# Revit family: LZWS-EDFPBM114K
name_source: partatom
category: Plumbing Fixtures
units: mm (PartAtom-declared; Revit-internal decimal feet)

## family parameters
Always vertical = Yes
Cut with Voids When Loaded = No
OmniClass Number = 23.45.00.00
OmniClass Title = Sanitary, Laundry, and Cleaning Equipment
Part Type = Normal
Room Calculation Point = No
Round Connector Dimension = Use Diameter
Shared = No
Work Plane-Based = No

## types (1)
- LZWS-EDFPBM114K
    Activation by = Electronic Bottle Filler Sensor with Mechanical Front Bubbler Button
    Approx. Shipping Weight = 121 lbs
    Assembly Code = D2010810
    Basin Material = 304 Stainless Steel
    Bubbler Style = Flexi-Guard ® Safety Bubbler
    Chilling Capacity = Non-refrigerated
    Description = Elkay ezH2O Bottle Filling Station with Integral SwirlFlo Fountain, Filtered Non-Refrigerated Stainless
    Dimensions (L x W x H) = 19-3/4 inch x 19 inch x 34-5/8 inch
    Finish = Stainless Steel
    Full Load Amps = 1
    Installation Location = Indoor
    Manufacturer = Elkay
    Model = LZWS-EDFPBM114K
    Mounting Type = Wall Mount (Inwall Frame/Plate)
    No. of Stations Served = 1
    Power = 115V/60Hz
    Rated Watts = 15
    Special Features = Antimicrobial, Filtered, Green Ticker™, Hands Free, Laminar Flow, Real Drain, Visual Filter Monitor
    Version = 1.0.0.0

## geometry (parser evidence)
native form markers: Sweep x10
no freeform markers — native parametric forms only
